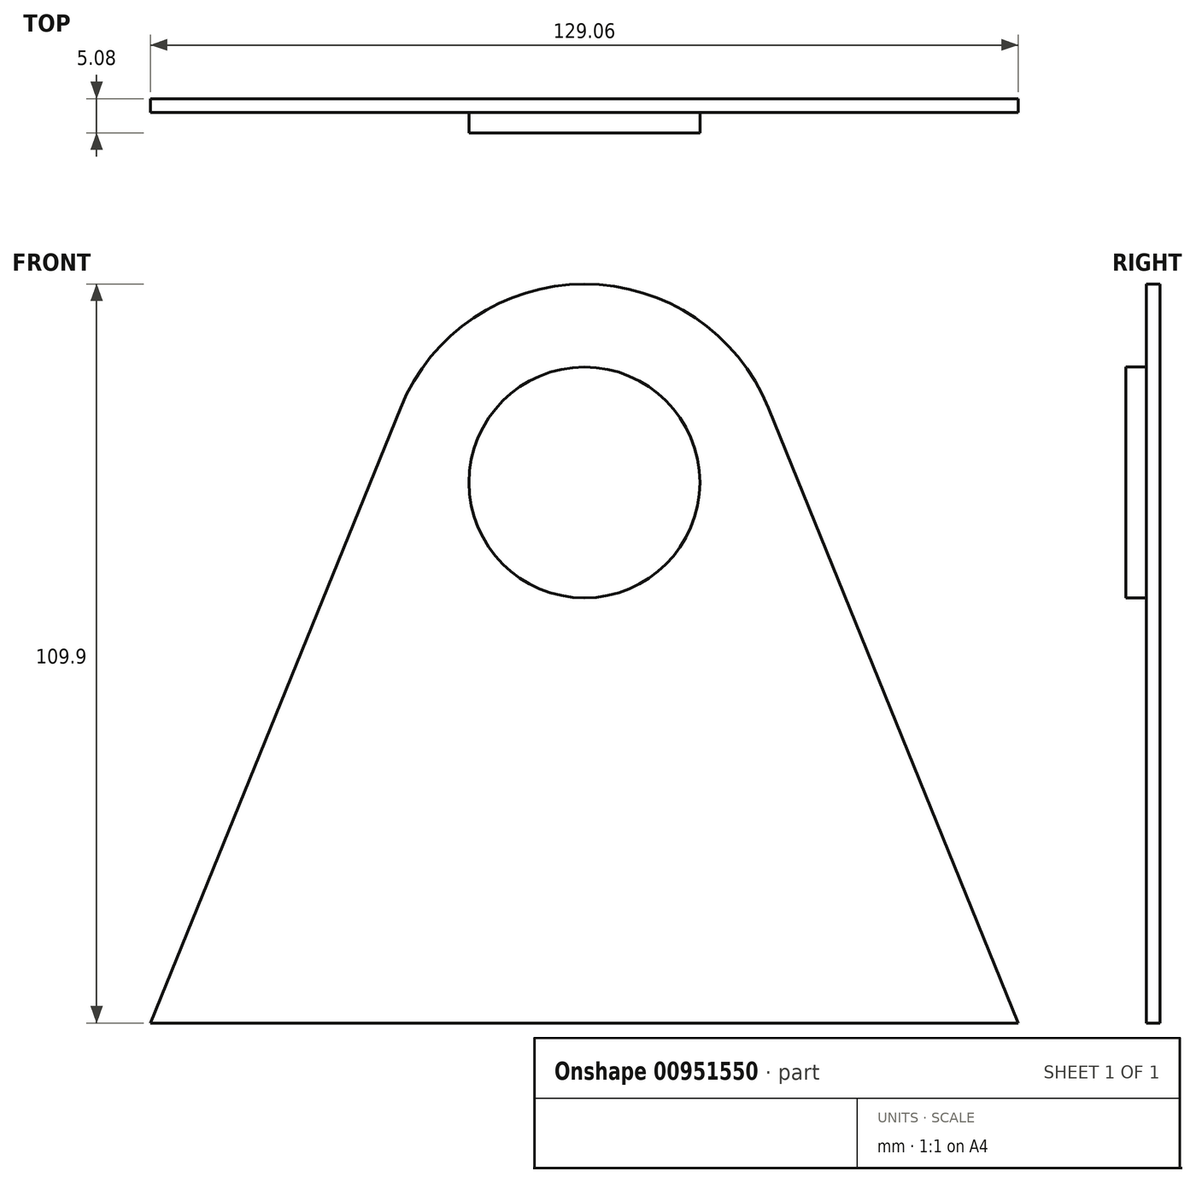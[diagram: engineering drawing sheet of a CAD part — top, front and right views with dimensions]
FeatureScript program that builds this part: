
annotation { "Feature Type Name" : "Feature", "Feature Type Description" : "" }
export const myFeature = defineFeature(function(context is Context, id is Id, definition is map)
    precondition{}
    {
        {
            var Q0;
            Q0=qCreatedBy(makeId("Front.planeOp"),FACE);
            var sketch = newSketch(context, id + "F0", { "sketchPlane" : qUnion([Q0])});
            skCircle(sketch, "E0", {"center": v(0, 0) * mm, "radius": 29.51 * mm});
            skLineSegment(sketch, "E1", {"start": v(-27.34, 11.11) * mm, "end": v(-64.53, -80.39) * mm});
            skLineSegment(sketch, "E2", {"start": v(-64.53, -80.39) * mm, "end": v(64.53, -80.39) * mm});
            skLineSegment(sketch, "E3", {"start": v(64.53, -80.39) * mm, "end": v(27.34, 11.11) * mm});
            skPoint(sketch, "E4", {"position": v(0, -80.39) * mm});
            skCircle(sketch, "E5", {"center": v(0, 0) * mm, "radius": 17.17 * mm});
            skSolve(sketch);
        }
        {
            var Q0;
            Q0=qSketchRegion(id+"F0",true);
            extrude(context, id + "F1", {"entities" : qUnion([Q0]), "depth" : 2.03 * mm, "offsetDistance" : 25.4 * mm});
        }
        {
            var Q0;
            Q0=makeQuery(id+"F0.imprint","IMPRINT",FACE,{"disambiguationData":[TD([[makeQuery(id+"F0.imprint","IMPRINT",EDGE,{"derivedFrom":sQuery(id+"F0.wireOp",EDGE,"E5")}),1.0]])]});
            extrude(context, id + "F2", {"entities" : qUnion([Q0]), "operationType" : NewBodyOperationType.ADD, "depth" : 5.08 * mm, "offsetDistance" : 25.4 * mm});
        }
    });
